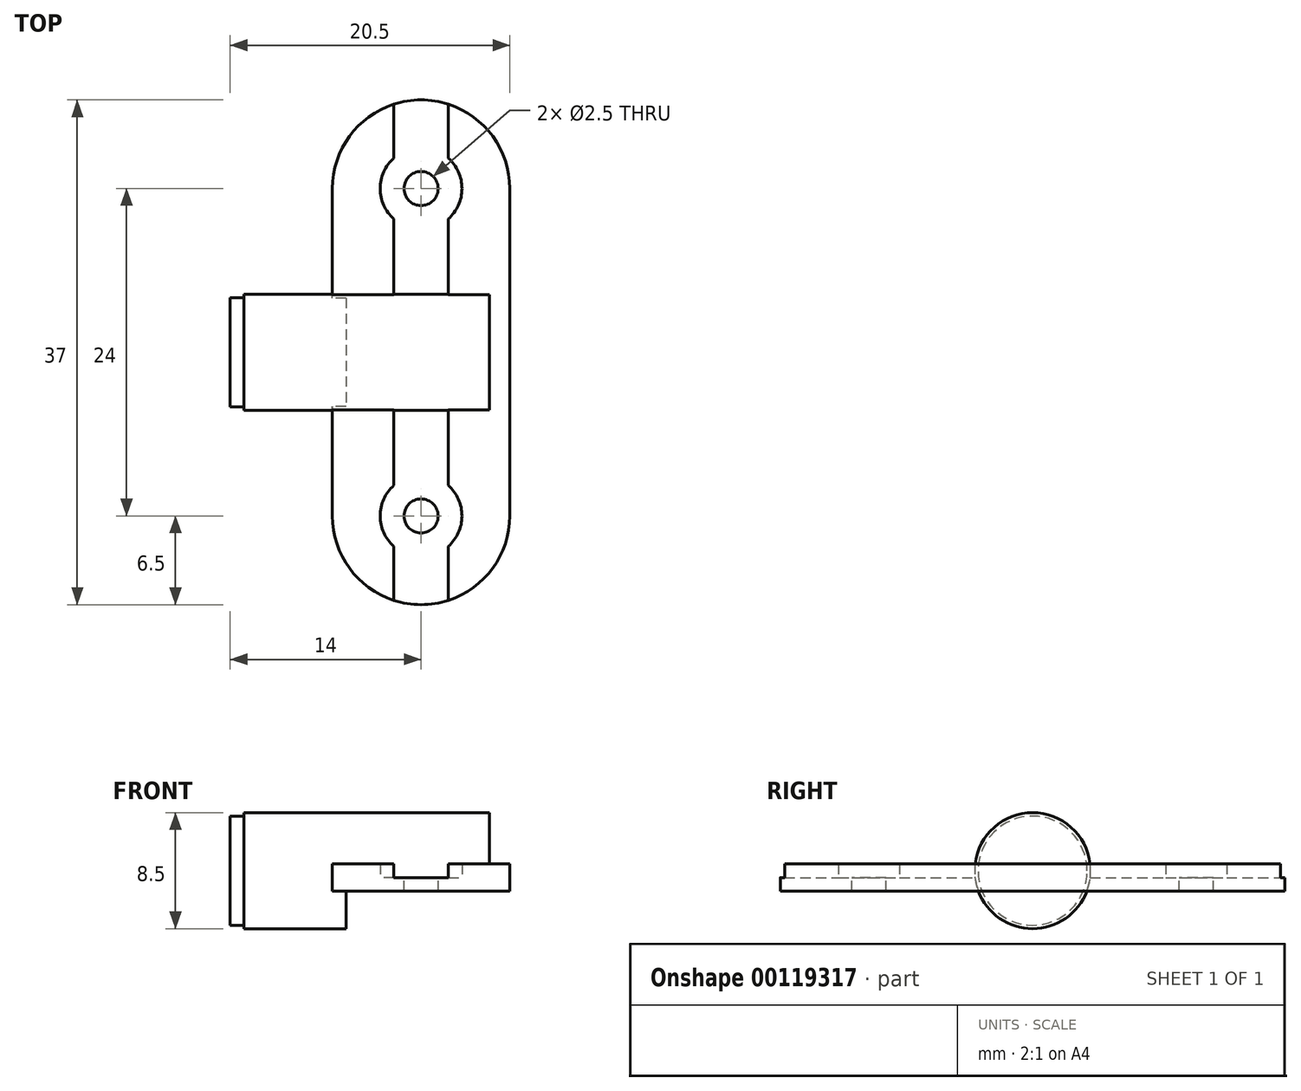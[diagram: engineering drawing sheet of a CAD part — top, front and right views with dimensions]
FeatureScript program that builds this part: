
annotation { "Feature Type Name" : "Feature", "Feature Type Description" : "" }
export const myFeature = defineFeature(function(context is Context, id is Id, definition is map)
    precondition{}
    {
        {
            var Q0;
            Q0=qCreatedBy(makeId("Top.planeOp"),FACE);
            var sketch = newSketch(context, id + "F0", { "sketchPlane" : qUnion([Q0])});
            skLineSegment(sketch, "E0.bottom", {"start": v(0, 18.5) * mm, "end": v(0, 18.5) * mm});
            skLineSegment(sketch, "E0.top", {"start": v(0, -18.5) * mm, "end": v(0, -18.5) * mm});
            skLineSegment(sketch, "E0.left", {"start": v(-6.5, 12) * mm, "end": v(-6.5, -12) * mm});
            skLineSegment(sketch, "E0.right", {"start": v(6.5, 12) * mm, "end": v(6.5, -12) * mm});
            skPoint(sketch, "E1.visualSharp", {"position": v(-6.5, 18.5) * mm});
            skArc(sketch, "E1.filletArc", {"start": v(0, 18.5) * mm, "mid": v(-4.6, 16.6) * mm, "end": v(-6.5, 12) * mm});
            skPoint(sketch, "E2.visualSharp", {"position": v(6.5, 18.5) * mm});
            skArc(sketch, "E2.filletArc", {"start": v(6.5, 12) * mm, "mid": v(4.6, 16.6) * mm, "end": v(0, 18.5) * mm});
            skPoint(sketch, "E3.visualSharp", {"position": v(6.5, -18.5) * mm});
            skArc(sketch, "E3.filletArc", {"start": v(0, -18.5) * mm, "mid": v(4.6, -16.6) * mm, "end": v(6.5, -12) * mm});
            skPoint(sketch, "E4.visualSharp", {"position": v(-6.5, -18.5) * mm});
            skArc(sketch, "E4.filletArc", {"start": v(-6.5, -12) * mm, "mid": v(-4.6, -16.6) * mm, "end": v(0, -18.5) * mm});
            skSolve(sketch);
        }
        {
            var Q0;
            Q0 = qSketchRegion(id + "F0", true);
            extrude(context, id + "F1", {"entities" : qUnion([Q0]), "depth" : 2 * mm});
        }
        {
            var Q0;
            Q0=makeQuery(id+"F1.opExtrude","CAP_FACE",FACE,{"disambiguationData":[OSD([sQuery(id+"F0.wireOp",EDGE,"E0.left"),sQuery(id+"F0.wireOp",EDGE,"E0.right"),sQuery(id+"F0.wireOp",EDGE,"E1.filletArc"),sQuery(id+"F0.wireOp",EDGE,"E2.filletArc"),sQuery(id+"F0.wireOp",EDGE,"E3.filletArc"),sQuery(id+"F0.wireOp",EDGE,"E4.filletArc")])],"isStart":false});
            var sketch = newSketch(context, id + "F2", { "sketchPlane" : qUnion([Q0])});
            skLineSegment(sketch, "E5", {"start": v(2, -20.14) * mm, "end": v(2, 20.65) * mm});
            skLineSegment(sketch, "E6.MirrorCS", {"start": v(-2, -20.14) * mm, "end": v(-2, 20.65) * mm});
            skLineSegment(sketch, "E7", {"start": v(2, -20.14) * mm, "end": v(-2, -20.14) * mm});
            skLineSegment(sketch, "E8", {"start": v(2, 20.65) * mm, "end": v(-2, 20.65) * mm});
            skSolve(sketch);
        }
        {
            var Q0;
            Q0 = qSketchRegion(id + "F2", true);
            extrude(context, id + "F3", {"entities" : qUnion([Q0]), "operationType" : NewBodyOperationType.REMOVE, "oppositeDirection" : true, "depth" : 1 * mm});
        }
        {
            var Q0;
            Q0=qCreatedBy(makeId("Right.planeOp"),FACE);
            cPlane(context, id + "F4", {"entities" : qUnion([Q0]), "cplaneType" : CPlaneType.OFFSET, "offset" : 14 * mm, "oppositeDirection" : true, "width" : 150 * mm, "height" : 150 * mm});
        }
        {
            var Q0;
            Q0=qCreatedBy(id+"F4.planeOp",FACE);
            var sketch = newSketch(context, id + "F5", { "sketchPlane" : qUnion([Q0])});
            skCircle(sketch, "E9", {"center": v(0, 1.5) * mm, "radius": 4.25 * mm});
            skSolve(sketch);
        }
        {
            var Q0;
            Q0 = qSketchRegion(id + "F5", true);
            extrude(context, id + "F6", {"entities" : qUnion([Q0]), "operationType" : NewBodyOperationType.ADD, "depth" : 19 * mm});
        }
        {
            var Q0;
            Q0=makeQuery(id+"F6.opExtrude","CAP_FACE",FACE,{"disambiguationData":[OSD([sQuery(id+"F5.wireOp",EDGE,"E9")])],"isStart":true});
            var sketch = newSketch(context, id + "F7", { "sketchPlane" : qUnion([Q0])});
            skLineSegment(sketch, "E10", {"start": v(-2.53, 1.5) * mm, "end": v(2.09, 1.5) * mm});
            skCircle(sketch, "E11", {"center": v(0, 1.5) * mm, "radius": 4 * mm});
            skCircle(sketch, "E12", {"center": v(0, 1.5) * mm, "radius": 4.4 * mm});
            skSolve(sketch);
        }
        {
            var Q0;
            Q0=makeQuery(id+"F7.imprint","IMPRINT",FACE,{"disambiguationData":[TD([[makeQuery(id+"F7.imprint","IMPRINT",EDGE,{"derivedFrom":sQuery(id+"F7.wireOp",EDGE,"E12")}),1.0]])]});
            var Q1;
            Q1=makeQuery(id+"F7.imprint","IMPRINT",FACE,{"disambiguationData":[TD([[makeQuery(id+"F7.imprint","IMPRINT",EDGE,{"derivedFrom":sQuery(id+"F7.wireOp",EDGE,"E11")}),-1.0]])]});
            extrude(context, id + "F8", {"entities" : qUnion([Q0, Q1]), "operationType" : NewBodyOperationType.REMOVE, "oppositeDirection" : true, "depth" : 1 * mm});
        }
        {
            var Q0;
            Q0=makeQuery(id+"F1.opExtrude","CAP_FACE",FACE,{"disambiguationData":[OSD([sQuery(id+"F0.wireOp",EDGE,"E0.left"),sQuery(id+"F0.wireOp",EDGE,"E0.right"),sQuery(id+"F0.wireOp",EDGE,"E1.filletArc"),sQuery(id+"F0.wireOp",EDGE,"E2.filletArc"),sQuery(id+"F0.wireOp",EDGE,"E3.filletArc"),sQuery(id+"F0.wireOp",EDGE,"E4.filletArc")])],"isStart":true});
            var sketch = newSketch(context, id + "F9", { "sketchPlane" : qUnion([Q0])});
            skLineSegment(sketch, "E13", {"start": v(-5.5, 5.94) * mm, "end": v(6.5, 5.94) * mm});
            skLineSegment(sketch, "E14", {"start": v(6.5, 5.94) * mm, "end": v(6.5, -7.05) * mm});
            skLineSegment(sketch, "E15", {"start": v(6.5, -7.05) * mm, "end": v(-5.5, -7.05) * mm});
            skLineSegment(sketch, "E16.0", {"start": v(-5.5, -7.05) * mm, "end": v(-5.5, 5.94) * mm});
            skSolve(sketch);
        }
        {
            var Q0;
            Q0 = qSketchRegion(id + "F9", true);
            extrude(context, id + "F10", {"entities" : qUnion([Q0]), "operationType" : NewBodyOperationType.REMOVE, "depth" : 25 * mm});
        }
        {
            var Q0;
            {var subQ0=sQuery(id+"F2.wireOp",EDGE,"E5");var subQ1=sQuery(id+"F2.wireOp",EDGE,"E6.MirrorCS");Q0=makeQuery(id+"F6.boolean.opBoolean","SPLIT",FACE,{"disambiguationData":[TD([makeQuery(id+"F1.opExtrude","SWEPT_FACE",FACE,{"disambiguationData":[OSD([sQuery(id+"F0.wireOp",EDGE,"E3.filletArc"),sQuery(id+"F0.wireOp",EDGE,"E4.filletArc")])]})])],"derivedFrom":makeQuery(id+"F3.boolean.opBoolean","COPY",FACE,{"derivedFrom":makeQuery(id+"F3.opExtrude","CAP_FACE",FACE,{"disambiguationData":[OSD([subQ0,subQ1,sQuery(id+"F2.wireOp",EDGE,"E7"),sQuery(id+"F2.wireOp",EDGE,"E8")])],"isStart":false})})});}
            var sketch = newSketch(context, id + "F11", { "sketchPlane" : qUnion([Q0])});
            skCircle(sketch, "E17", {"center": v(0, -12) * mm, "radius": 3 * mm});
            skCircle(sketch, "E18.MirrorC", {"center": v(0, 12) * mm, "radius": 3 * mm});
            skSolve(sketch);
        }
        {
            var Q0;
            Q0 = qSketchRegion(id + "F11", true);
            var Q1;
            {var subQ0=sQuery(id+"F0.wireOp",EDGE,"E0.left");var subQ1=makeQuery(id+"F1.opExtrude","SWEPT_FACE",FACE,{"disambiguationData":[OSD([subQ0])]});var subQ2=sQuery(id+"F0.wireOp",EDGE,"E2.filletArc");var subQ3=sQuery(id+"F0.wireOp",EDGE,"E1.filletArc");var subQ4=makeQuery(id+"F1.opExtrude","SWEPT_FACE",FACE,{"disambiguationData":[OSD([subQ3,subQ2])]});var subQ6=sQuery(id+"F0.wireOp",EDGE,"E4.filletArc");var subQ7=sQuery(id+"F0.wireOp",EDGE,"E3.filletArc");Q1=makeQuery(id+"F6.boolean.opBoolean","SPLIT",FACE,{"disambiguationData":[TD([subQ4])],"derivedFrom":makeQuery(id+"F3.boolean.opBoolean","SPLIT",FACE,{"disambiguationData":[TD([subQ1])],"derivedFrom":makeQuery(id+"F1.opExtrude","CAP_FACE",FACE,{"disambiguationData":[OSD([subQ0,sQuery(id+"F0.wireOp",EDGE,"E0.right"),subQ3,subQ2,subQ7,subQ6])],"isStart":false})})});}
            extrude(context, id + "F12", {"entities" : qUnion([Q0]), "operationType" : NewBodyOperationType.REMOVE, "endBound" : BoundingType.UP_TO_SURFACE, "endBoundEntityFace" : qUnion([Q1]), "depth" : 25 * mm});
        }
        {
            var Q0;
            {var subQ0=sQuery(id+"F2.wireOp",EDGE,"E5");var subQ1=sQuery(id+"F2.wireOp",EDGE,"E6.MirrorCS");Q0=makeQuery(id+"F12.boolean.opBoolean","MERGE",FACE,{"derivedFrom":[makeQuery(id+"F6.boolean.opBoolean","SPLIT",FACE,{"disambiguationData":[TD([makeQuery(id+"F1.opExtrude","SWEPT_FACE",FACE,{"disambiguationData":[OSD([sQuery(id+"F0.wireOp",EDGE,"E3.filletArc"),sQuery(id+"F0.wireOp",EDGE,"E4.filletArc")])]})])],"derivedFrom":makeQuery(id+"F3.boolean.opBoolean","COPY",FACE,{"derivedFrom":makeQuery(id+"F3.opExtrude","CAP_FACE",FACE,{"disambiguationData":[OSD([subQ0,subQ1,sQuery(id+"F2.wireOp",EDGE,"E7"),sQuery(id+"F2.wireOp",EDGE,"E8")])],"isStart":false})})}),makeQuery(id+"F12.opExtrude","CAP_FACE",FACE,{"disambiguationData":[OSD([sQuery(id+"F11.wireOp",EDGE,"E17")])],"isStart":true})]});}
            var sketch = newSketch(context, id + "F13", { "sketchPlane" : qUnion([Q0])});
            skCircle(sketch, "E19", {"center": v(0, -12) * mm, "radius": 1.25 * mm});
            skSolve(sketch);
        }
        {
            var Q0;
            Q0 = qSketchRegion(id + "F13", true);
            extrude(context, id + "F14", {"entities" : qUnion([Q0]), "operationType" : NewBodyOperationType.REMOVE, "endBound" : BoundingType.THROUGH_ALL, "oppositeDirection" : true, "depth" : 25 * mm});
        }
        {
            var Q0;
            {var subQ0=sQuery(id+"F2.wireOp",EDGE,"E5");var subQ1=sQuery(id+"F2.wireOp",EDGE,"E6.MirrorCS");Q0=makeQuery(id+"F12.boolean.opBoolean","MERGE",FACE,{"derivedFrom":[makeQuery(id+"F6.boolean.opBoolean","SPLIT",FACE,{"disambiguationData":[TD([makeQuery(id+"F1.opExtrude","SWEPT_FACE",FACE,{"disambiguationData":[OSD([sQuery(id+"F0.wireOp",EDGE,"E1.filletArc"),sQuery(id+"F0.wireOp",EDGE,"E2.filletArc")])]})])],"derivedFrom":makeQuery(id+"F3.boolean.opBoolean","COPY",FACE,{"derivedFrom":makeQuery(id+"F3.opExtrude","CAP_FACE",FACE,{"disambiguationData":[OSD([subQ0,subQ1,sQuery(id+"F2.wireOp",EDGE,"E7"),sQuery(id+"F2.wireOp",EDGE,"E8")])],"isStart":false})})}),makeQuery(id+"F12.opExtrude","CAP_FACE",FACE,{"disambiguationData":[OSD([sQuery(id+"F11.wireOp",EDGE,"E18.MirrorC")])],"isStart":true})]});}
            var sketch = newSketch(context, id + "F15", { "sketchPlane" : qUnion([Q0])});
            skCircle(sketch, "E20", {"center": v(0, 12) * mm, "radius": 1.25 * mm});
            skSolve(sketch);
        }
        {
            var Q0;
            Q0 = qSketchRegion(id + "F15", true);
            extrude(context, id + "F16", {"entities" : qUnion([Q0]), "operationType" : NewBodyOperationType.REMOVE, "endBound" : BoundingType.THROUGH_ALL, "oppositeDirection" : true, "depth" : 25 * mm});
        }
    });
